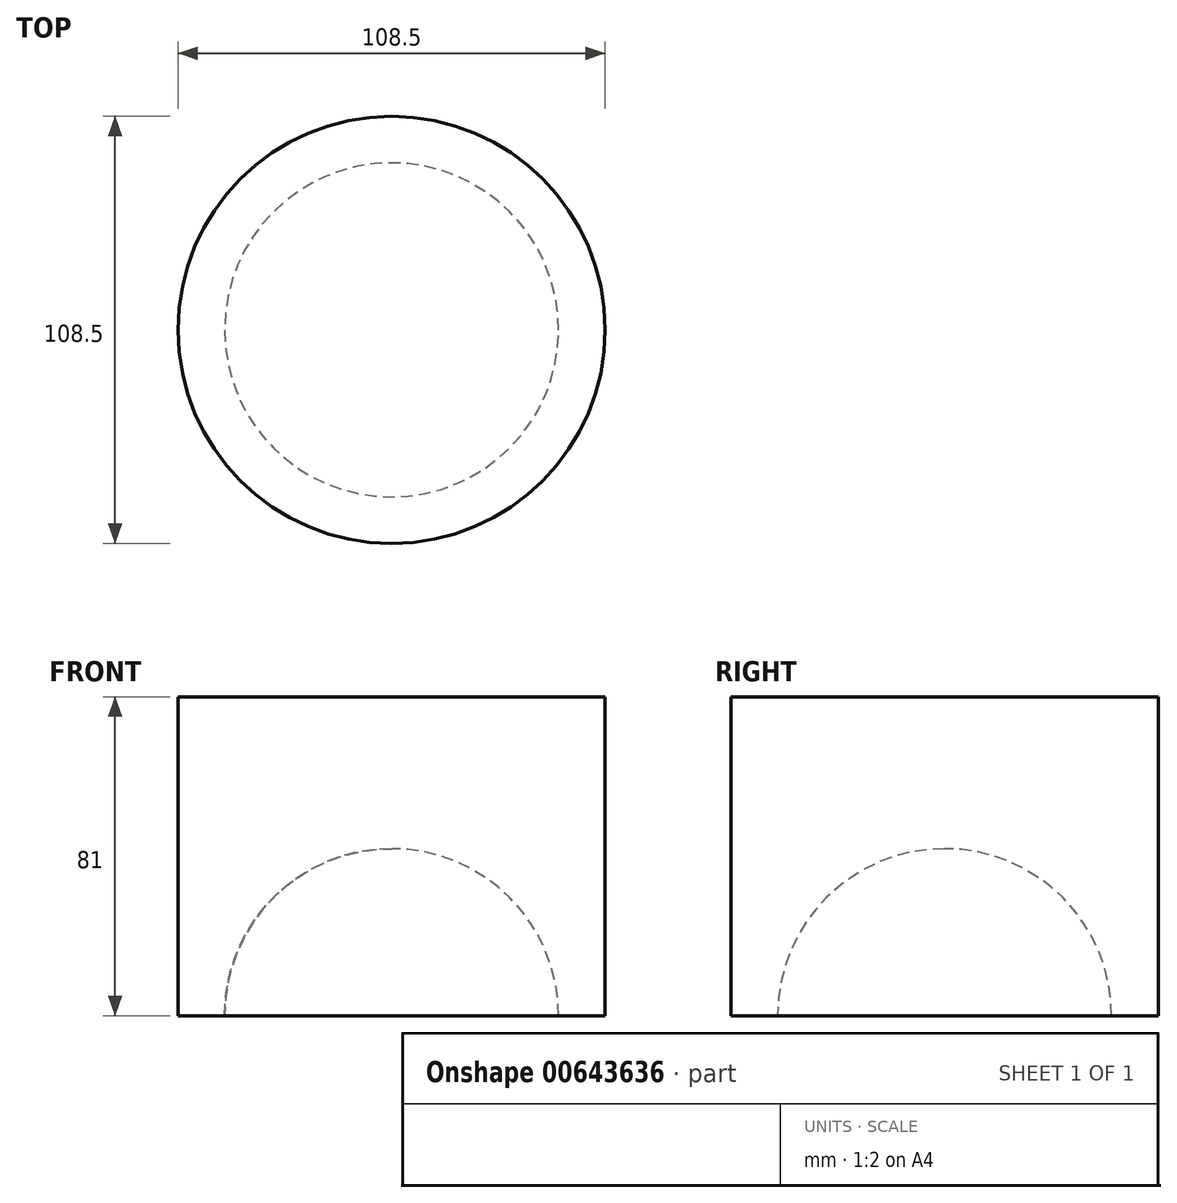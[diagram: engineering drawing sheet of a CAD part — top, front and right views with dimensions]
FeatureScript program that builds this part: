
annotation { "Feature Type Name" : "Feature", "Feature Type Description" : "" }
export const myFeature = defineFeature(function(context is Context, id is Id, definition is map)
    precondition{}
    {
        {
            var Q0;
            Q0=qCreatedBy(makeId("Top.planeOp"),FACE);
            var sketch = newSketch(context, id + "F0", { "sketchPlane" : qUnion([Q0])});
            skCircle(sketch, "E0", {"center": v(0, 0) * mm, "radius": 54.25 * mm});
            skSolve(sketch);
        }
        {
            var Q0;
            Q0=makeQuery(id+"F0.imprint","IMPRINT",FACE,{"disambiguationData":[TD([[makeQuery(id+"F0.imprint","IMPRINT",EDGE,{"derivedFrom":sQuery(id+"F0.wireOp",EDGE,"E0")}),1.0]])]});
            extrude(context, id + "F1", {"entities" : qUnion([Q0]), "depth" : 81 * mm, "offsetDistance" : 25 * mm});
        }
        {
            var Q0;
            Q0=qCreatedBy(makeId("Front.planeOp"),FACE);
            var sketch = newSketch(context, id + "F2", { "sketchPlane" : qUnion([Q0])});
            skArc(sketch, "E1", {"start": v(0, 42.43) * mm, "mid": v(-42.43, 0) * mm, "end": v(0, -42.43) * mm});
            skLineSegment(sketch, "E2", {"start": v(0, -42.43) * mm, "end": v(0, 42.43) * mm});
            skSolve(sketch);
        }
        {
            var Q0;
            Q0=makeQuery(id+"F2.imprint","IMPRINT",FACE,{"disambiguationData":[TD([[makeQuery(id+"F2.imprint","IMPRINT",EDGE,{"derivedFrom":sQuery(id+"F2.wireOp",EDGE,"E1")}),1.0]])]});
            var Q1;
            Q1=sQuery(id+"F2.wireOp",EDGE,"E2");
            revolve(context, id + "F3", {"operationType" : NewBodyOperationType.REMOVE, "entities" : qUnion([Q0]), "axis" : qUnion([Q1]), "revolveType" : RevolveType.FULL, "oppositeDirection" : true});
        }
    });
